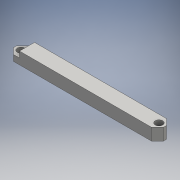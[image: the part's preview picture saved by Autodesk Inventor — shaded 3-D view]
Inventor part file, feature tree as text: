
AUTODESK INVENTOR PART (.ipt)
format: ipt  version: 2016 (Build 200138000, 138)  size: 127,488 bytes
history: native  units: mm
features: extrude x4, chamfer x4, sketch x4, other x1
ambient origin geometry x8: Origin, YZ Plane, XZ Plane, XY Plane, X Axis, Y Axis, Z Axis, Center Point
bodies: Body1 (feature_tree)
feature tree (13):
  other  "ソリッド1"
  extrude  "押し出し1"  Depth=50.0mm
  extrude  "押し出し2"  Depth=4.0mm
  chamfer  "面取り1"  Distance=5.0mm
  chamfer  "面取り2"  Distance=2.5mm
  extrude  "押し出し3"  Depth=2.0mm
  chamfer  "面取り3"  Distance=5.0mm
  chamfer  "面取り4"  Distance=2.0mm Angle=45.0deg
  extrude  "押し出し4"  Depth=2.0mm TaperAngle=45.0deg
  sketch  "スケッチ1"
  sketch  "スケッチ2"
  sketch  "スケッチ3"
  sketch  "スケッチ4"
